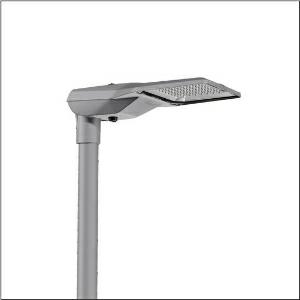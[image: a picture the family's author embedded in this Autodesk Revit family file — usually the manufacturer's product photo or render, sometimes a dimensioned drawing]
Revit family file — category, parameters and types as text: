
# Revit family: streetlight_sl_21_midi___pc-l_5xe3f33t08mb_a9f3
name_source: partatom
category: Lighting Fixtures
units: mm (PartAtom-declared; Revit-internal decimal feet)

## family parameters
Cut with Voids When Loaded = No
Host = Face
Light Source = No
Part Type = Normal
Room Calculation Point = No
Round Connector Dimension = Use Diameter
Shared = No

## types (1)
- --- (1 x LED, 17390 lm, 136 W, 3000K)
    Apparent Load = 136 VA
    CIE Flux Codes = 38 78 98 100 100
    Color Rendering = 70
    Color Temperature = 3000K
    Default Elevation = 1800 mm
    Description = Streetlight SL 21 midi, mast luminaire, primary light control with lens, of PMMA, primary optical cover: cover, of toughened safety glass, transparent, light distribution: PC-L, light emission: direct distribution, primary light characteristic: asymmetric, left, installation type: side-entry, post-top, LED, High Power LED, rated luminous flux: 17.390lm, luminous efficacy: 128lm/W, light colour: 730, colour temperature: 3000K, control gear: D4i, control: overheat protection, constant luminous flux control, time-dependent luminous flux control, flexible luminous flux parameterisation, pre-setting: logarithmic dimming characteristic, mains connection: 230..240V, AC, 50/60Hz, start of lifetime: 136W, end of service life: 142W, reduction: 61W, luminaire housing, of diecast aluminium, powder-coated, SITECO metallic grey (DB 702S), corrosivity category C5 high according to DIN EN ISO 12944, please order mast flange separately, inclination adjustable: 0°, 5°, 10°, 15°, sealing non-destructively replaceable, multi-level sealing system, length: 644mm, width: 335mm, height: 110mm, mast flange for spigot size: 42mm (side-entry): 5XC10008XM4, 60/48mm (side-entry/post-top): 5XC10108XM2, 76/60mm (side-entry/post-top): 5XC10108XM1, mounting height: 4..8m, Smart Interface below and above, protection rating (complete): IP66, insulation class (complete): insulation class II (safety insulation), certification: CE, ENEC, ENEC+, VDE, impact resistance: IK10, permissible operating ambient temperature for outdoor applications: -40..+50°C, standard-compliant lighting for roads and squares, packaging unit: 1 piece

Light Distribution: PC-L
    Height = 111 mm
    Lamp = 1 x LED
    Lamp Light Flux = 17390 lm
    Lamp Power = 136 W
    Lamp count = 1
    Length = 644 mm
    Luminous efficacy = 128 lm/W
    Manufacturer = Siteco
    ModVariant = No
    Model = 5XE3F33T08MB
    Number of Poles = 1
    OnlyDefault = Yes
    Power Factor = 1
    Product Name = Streetlight SL 21 midi | PC-L
    Product group = mast luminaire | pylon top
    ProductGroupID = 6100
    Protection Class = Protection class II
    Protection Degree = IP 66
    RLX_Detail_Level = 1
    RLX_Emergency_Light_Flux = 0 lm
    RLX_Emergency_Type = 0
    RLX_Emergency_Type_DB = No
    RlxData = <blob elided: 29609 chars, md5=6411c4c8>
    Socket = socket
    Standby Power = 0 W
    System Light Flux = 17390 lm
    System Power = 136 W
    Type Comments = factory setting: luminous flux: 100 % | dim-lin: 254 | 695 mA
    Type Image = l_1004304.jpg
    URL = http://relux.com
    VarID = @adj_072155
    Voltage = 0 V
    Weight = 0.00 kg
    Width = 336 mm

## geometry (parser evidence)
native form markers: Blend x4, Sweep x9
no freeform markers — native parametric forms only
